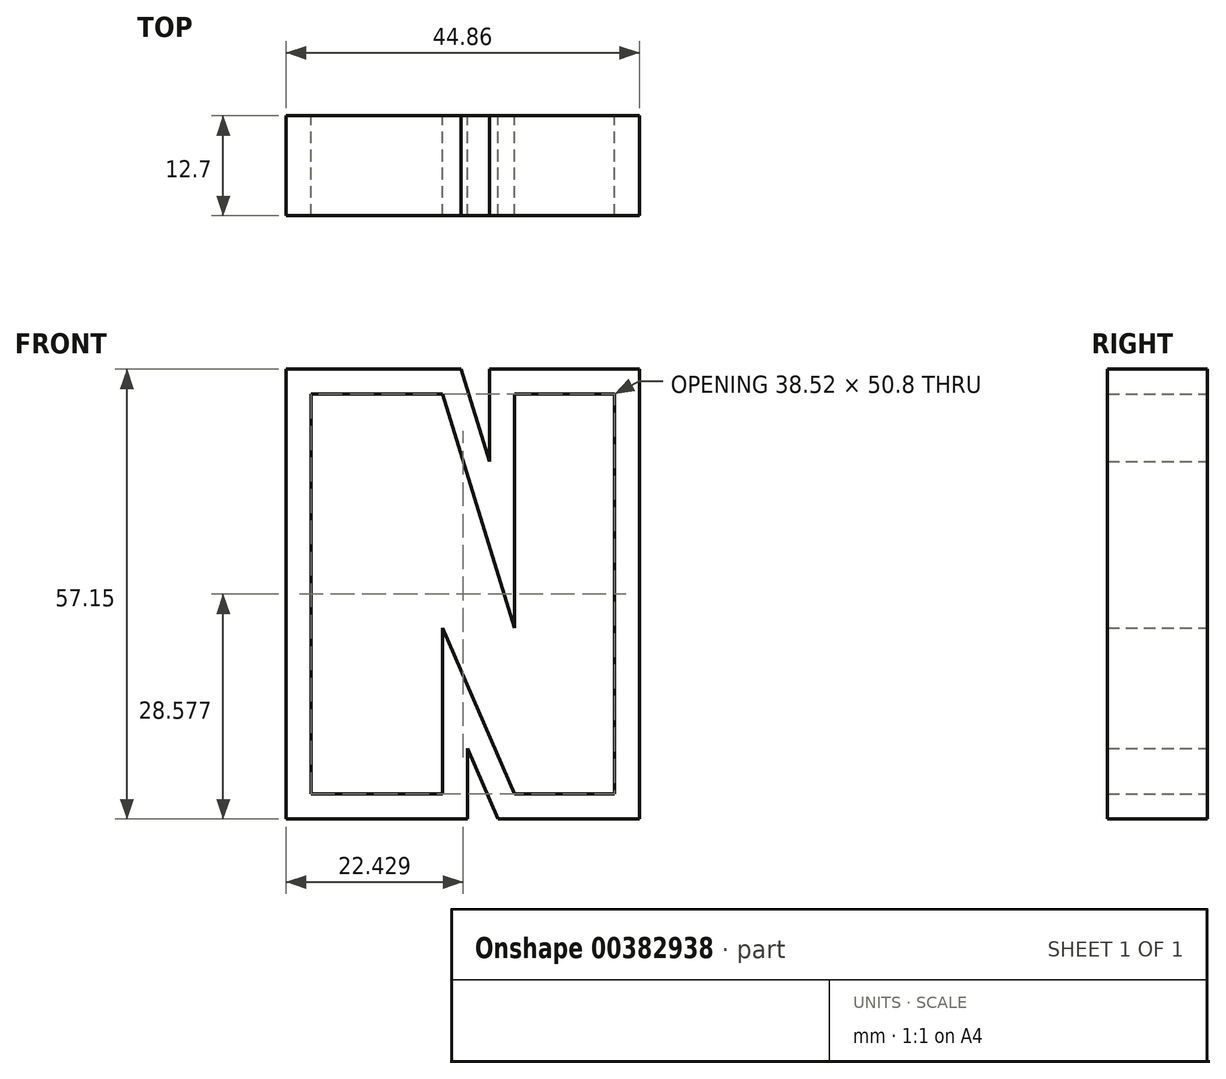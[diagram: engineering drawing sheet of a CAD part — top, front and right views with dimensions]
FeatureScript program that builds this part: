
annotation { "Feature Type Name" : "Feature", "Feature Type Description" : "" }
export const myFeature = defineFeature(function(context is Context, id is Id, definition is map)
    precondition{}
    {
        {
            var Q0;
            Q0=qCreatedBy(makeId("Front.planeOp"),FACE);
            var sketch = newSketch(context, id + "F0", { "sketchPlane" : qUnion([Q0])});
            skLineSegment(sketch, "E0", {"start": v(-53.63, -6.4) * mm, "end": v(-36.95, -6.4) * mm});
            skLineSegment(sketch, "E1", {"start": v(-53.63, -6.4) * mm, "end": v(-53.63, 44.4) * mm});
            skLineSegment(sketch, "E2", {"start": v(-53.63, 44.4) * mm, "end": v(-36.95, 44.4) * mm});
            skLineSegment(sketch, "E3", {"start": v(-36.95, -6.4) * mm, "end": v(-36.95, 14.7) * mm});
            skLineSegment(sketch, "E4", {"start": v(-36.95, 14.7) * mm, "end": v(-27.81, -6.4) * mm});
            skLineSegment(sketch, "E5", {"start": v(-27.81, -6.4) * mm, "end": v(-15.11, -6.4) * mm});
            skLineSegment(sketch, "E6", {"start": v(-15.11, -6.4) * mm, "end": v(-15.11, 44.4) * mm});
            skLineSegment(sketch, "E7", {"start": v(-15.11, 44.4) * mm, "end": v(-27.81, 44.4) * mm});
            skLineSegment(sketch, "E8", {"start": v(-27.81, 44.4) * mm, "end": v(-27.81, 14.7) * mm});
            skLineSegment(sketch, "E9", {"start": v(-27.81, 14.7) * mm, "end": v(-36.95, 44.4) * mm});
            skLineSegment(sketch, "E10.0", {"start": v(-56.8, 47.57) * mm, "end": v(-34.6, 47.57) * mm});
            skLineSegment(sketch, "E10.1", {"start": v(-56.8, -9.58) * mm, "end": v(-56.8, 47.57) * mm});
            skLineSegment(sketch, "E10.2", {"start": v(-56.8, -9.58) * mm, "end": v(-33.77, -9.58) * mm});
            skLineSegment(sketch, "E10.3", {"start": v(-33.77, -9.58) * mm, "end": v(-33.77, -0.62) * mm});
            skLineSegment(sketch, "E10.4", {"start": v(-33.77, -0.62) * mm, "end": v(-29.9, -9.58) * mm});
            skLineSegment(sketch, "E10.5", {"start": v(-29.9, -9.58) * mm, "end": v(-11.94, -9.58) * mm});
            skLineSegment(sketch, "E10.6", {"start": v(-30.99, 35.82) * mm, "end": v(-35.29, 49.8) * mm});
            skLineSegment(sketch, "E10.7", {"start": v(-30.99, 47.57) * mm, "end": v(-30.99, 35.82) * mm});
            skLineSegment(sketch, "E10.8", {"start": v(-11.94, 47.57) * mm, "end": v(-30.99, 47.57) * mm});
            skLineSegment(sketch, "E10.9", {"start": v(-11.94, -9.58) * mm, "end": v(-11.94, 47.57) * mm});
            skSolve(sketch);
        }
        {
            var Q0;
            Q0=makeQuery(id+"F0.imprint","IMPRINT",FACE,{"disambiguationData":[TD([[makeQuery(id+"F0.imprint","IMPRINT",EDGE,{"derivedFrom":sQuery(id+"F0.wireOp",EDGE,"E0")}),-1.0]])]});
            extrude(context, id + "F1", {"entities" : qUnion([Q0]), "depth" : 12.7 * mm});
        }
    });
